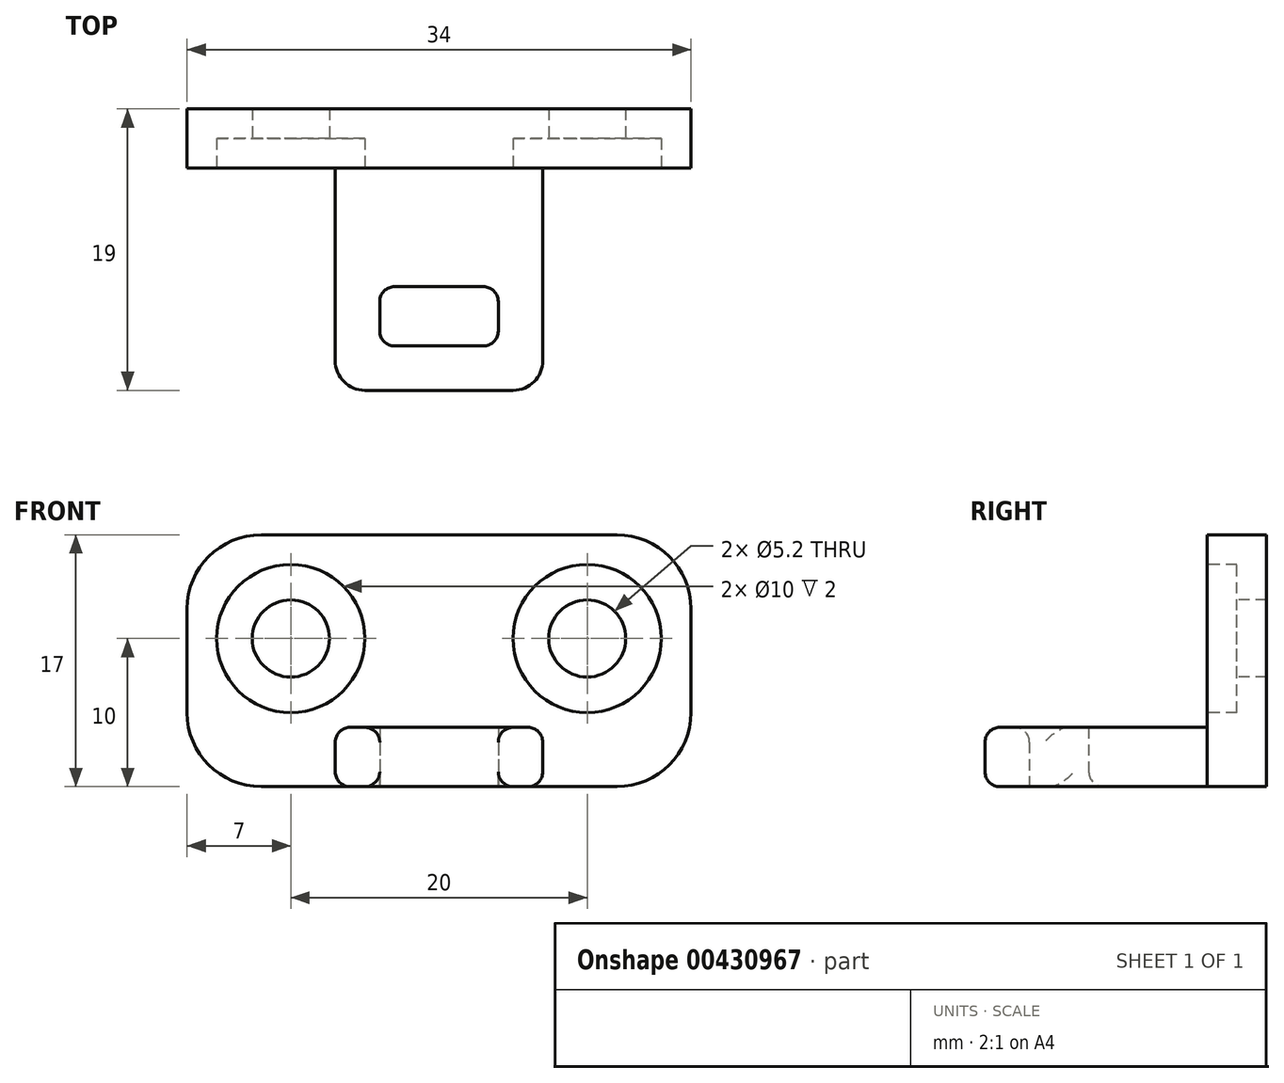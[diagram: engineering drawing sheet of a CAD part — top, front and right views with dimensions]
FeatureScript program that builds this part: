
annotation { "Feature Type Name" : "Feature", "Feature Type Description" : "" }
export const myFeature = defineFeature(function(context is Context, id is Id, definition is map)
    precondition{}
    {
        {
            var Q0;
            Q0=qCreatedBy(makeId("Top.planeOp"),FACE);
            var sketch = newSketch(context, id + "F0", { "sketchPlane" : qUnion([Q0])});
            skLineSegment(sketch, "E0.bottom", {"start": v(0, 0) * mm, "end": v(50, 0) * mm, "construction": true});
            skLineSegment(sketch, "E0.top", {"start": v(0, 20) * mm, "end": v(50, 20) * mm, "construction": true});
            skLineSegment(sketch, "E0.left", {"start": v(0, 0) * mm, "end": v(0, 20) * mm, "construction": true});
            skLineSegment(sketch, "E0.right", {"start": v(50, 0) * mm, "end": v(50, 20) * mm, "construction": true});
            skLineSegment(sketch, "E1.bottom", {"start": v(21, -8) * mm, "end": v(29, -8) * mm});
            skLineSegment(sketch, "E1.top", {"start": v(21, -12) * mm, "end": v(29, -12) * mm});
            skLineSegment(sketch, "E1.left", {"start": v(21, -8) * mm, "end": v(21, -12) * mm});
            skLineSegment(sketch, "E1.right", {"start": v(29, -8) * mm, "end": v(29, -12) * mm});
            skPoint(sketch, "E2", {"position": v(25, -8) * mm});
            skPoint(sketch, "E3", {"position": v(25, 0) * mm});
            skLineSegment(sketch, "E4.bottom", {"start": v(32, -15) * mm, "end": v(18, -15) * mm});
            skLineSegment(sketch, "E4.top", {"start": v(32, 0) * mm, "end": v(18, 0) * mm});
            skLineSegment(sketch, "E4.left", {"start": v(32, -15) * mm, "end": v(32, 0) * mm});
            skLineSegment(sketch, "E4.right", {"start": v(18, -15) * mm, "end": v(18, 0) * mm});
            skSolve(sketch);
        }
        {
            var Q0;
            Q0=makeQuery(id+"F0.imprint","IMPRINT",FACE,{"disambiguationData":[TD([[makeQuery(id+"F0.imprint","IMPRINT",EDGE,{"derivedFrom":sQuery(id+"F0.wireOp",EDGE,"E1.bottom")}),1.0]])]});
            extrude(context, id + "F1", {"entities" : qUnion([Q0]), "depth" : 4 * mm});
        }
        {
            var Q0;
            Q0=makeQuery(id+"F1.opExtrude","SWEPT_FACE",FACE,{"disambiguationData":[OSD([sQuery(id+"F0.wireOp",EDGE,"E4.top")])]});
            var sketch = newSketch(context, id + "F2", { "sketchPlane" : qUnion([Q0])});
            skLineSegment(sketch, "E5.bottom", {"start": v(0, 0) * mm, "end": v(-50, 0) * mm, "construction": true});
            skLineSegment(sketch, "E5.top", {"start": v(0, 20) * mm, "end": v(-50, 20) * mm, "construction": true});
            skLineSegment(sketch, "E5.left", {"start": v(0, 0) * mm, "end": v(0, 20) * mm, "construction": true});
            skLineSegment(sketch, "E5.right", {"start": v(-50, 0) * mm, "end": v(-50, 20) * mm, "construction": true});
            skPoint(sketch, "E6", {"position": v(0, 10) * mm});
            skLineSegment(sketch, "E7.bottom", {"start": v(-42, 0) * mm, "end": v(-8, 0) * mm});
            skLineSegment(sketch, "E7.top", {"start": v(-42, 17) * mm, "end": v(-8, 17) * mm});
            skLineSegment(sketch, "E7.left", {"start": v(-42, 0) * mm, "end": v(-42, 17) * mm});
            skLineSegment(sketch, "E7.right", {"start": v(-8, 0) * mm, "end": v(-8, 17) * mm});
            skPoint(sketch, "E8", {"position": v(-25, 17) * mm});
            skPoint(sketch, "E9", {"position": v(-15, 10) * mm});
            skPoint(sketch, "E10", {"position": v(-35, 10) * mm});
            skSolve(sketch);
        }
        {
            var Q0;
            Q0=makeQuery(id+"F2.imprint","IMPRINT",FACE,{"disambiguationData":[TD([[makeQuery(id+"F2.imprint","IMPRINT",EDGE,{"derivedFrom":sQuery(id+"F2.wireOp",EDGE,"E7.top")}),-1.0]])]});
            var Q1;
            {var subQ1=sQuery(id+"F0.wireOp",EDGE,"E4.top");Q1=makeQuery(id+"F2.imprint","IMPRINT",FACE,{"disambiguationData":[TD([[makeQuery(id+"F2.imprint","IMPRINT",EDGE,{"derivedFrom":makeQuery(id+"F1.opExtrude","CAP_EDGE",EDGE,{"disambiguationData":[OSD([subQ1])],"isStart":false})}),-1.0]])]});}
            extrude(context, id + "F3", {"entities" : qUnion([Q0, Q1]), "operationType" : NewBodyOperationType.ADD, "depth" : 4 * mm});
        }
        {
            var Q0;
            Q0=sQuery(id+"F2.wireOp",VERTEX,"E9");
            var Q1;
            Q1=sQuery(id+"F2.wireOp",VERTEX,"E10");
            var Q2;
            Q2=makeQuery(id+"F1.opExtrude","SWEPT_BODY",BODY,{"disambiguationData":[OSD([sQuery(id+"F0.wireOp",EDGE,"E1.bottom"),sQuery(id+"F0.wireOp",EDGE,"E1.top"),sQuery(id+"F0.wireOp",EDGE,"E1.left"),sQuery(id+"F0.wireOp",EDGE,"E1.right"),sQuery(id+"F0.wireOp",EDGE,"E4.bottom"),sQuery(id+"F0.wireOp",EDGE,"E4.top"),sQuery(id+"F0.wireOp",EDGE,"E4.left"),sQuery(id+"F0.wireOp",EDGE,"E4.right")])]});
            hole(context, id + "F4", {"style" : HoleStyle.C_BORE, "endStyle" : HoleEndStyle.THROUGH, "oppositeDirection" : true, "holeDiameter" : 5.2 * mm, "cBoreDiameter" : 10 * mm, "cBoreDepth" : 2 * mm, "tappedDepth" : 12 * mm, "tapClearance" : 3, "locations" : qUnion([Q0, Q1]), "scope" : qUnion([Q2])});
        }
        {
            var Q0;
            Q0=makeQuery(id+"F1.opExtrude","SWEPT_EDGE",EDGE,{"disambiguationData":[OSD([sQuery(id+"F0.wireOp",EDGE,"E4.bottom"),sQuery(id+"F0.wireOp",EDGE,"E4.right")])]});
            var Q1;
            Q1=makeQuery(id+"F1.opExtrude","SWEPT_EDGE",EDGE,{"disambiguationData":[OSD([sQuery(id+"F0.wireOp",EDGE,"E4.bottom"),sQuery(id+"F0.wireOp",EDGE,"E4.left")])]});
            fillet(context, id + "F5", {"entities" : qUnion([Q0, Q1]), "radius" : 2 * mm, "tangentPropagation" : true, "allowEdgeOverflow" : false});
        }
        {
            var Q0;
            Q0=makeQuery(id+"F1.opExtrude","SWEPT_EDGE",EDGE,{"disambiguationData":[OSD([sQuery(id+"F0.wireOp",EDGE,"E4.top"),sQuery(id+"F0.wireOp",EDGE,"E4.right")])]});
            var Q1;
            Q1=makeQuery(id+"F1.opExtrude","SWEPT_EDGE",EDGE,{"disambiguationData":[OSD([sQuery(id+"F0.wireOp",EDGE,"E4.top"),sQuery(id+"F0.wireOp",EDGE,"E4.left")])]});
            var Q2;
            Q2=makeQuery(id+"F1.opExtrude","CAP_EDGE",EDGE,{"disambiguationData":[OSD([sQuery(id+"F0.wireOp",EDGE,"E4.top")])],"isStart":false});
            var Q3;
            Q3=makeQuery(id+"F3.opExtrude","SWEPT_EDGE",EDGE,{"disambiguationData":[OSD([sQuery(id+"F2.wireOp",EDGE,"E7.top"),sQuery(id+"F2.wireOp",EDGE,"E7.left")])]});
            var Q4;
            Q4=makeQuery(id+"F3.opExtrude","SWEPT_EDGE",EDGE,{"disambiguationData":[OSD([sQuery(id+"F2.wireOp",EDGE,"E7.top"),sQuery(id+"F2.wireOp",EDGE,"E7.right")])]});
            var Q5;
            Q5=makeQuery(id+"F3.opExtrude","SWEPT_EDGE",EDGE,{"disambiguationData":[OSD([sQuery(id+"F2.wireOp",EDGE,"E7.bottom"),sQuery(id+"F2.wireOp",EDGE,"E7.left")])]});
            var Q6;
            Q6=makeQuery(id+"F3.opExtrude","SWEPT_EDGE",EDGE,{"disambiguationData":[OSD([sQuery(id+"F2.wireOp",EDGE,"E7.bottom"),sQuery(id+"F2.wireOp",EDGE,"E7.right")])]});
            fillet(context, id + "F6", {"entities" : qUnion([Q0, Q1, Q2, Q3, Q4, Q5, Q6]), "radius" : 5 * mm, "tangentPropagation" : true, "allowEdgeOverflow" : false});
        }
        {
            var Q0;
            Q0=makeQuery(id+"F1.opExtrude","SWEPT_EDGE",EDGE,{"disambiguationData":[OSD([sQuery(id+"F0.wireOp",EDGE,"E1.bottom"),sQuery(id+"F0.wireOp",EDGE,"E1.left")])]});
            var Q1;
            Q1=makeQuery(id+"F1.opExtrude","SWEPT_EDGE",EDGE,{"disambiguationData":[OSD([sQuery(id+"F0.wireOp",EDGE,"E1.bottom"),sQuery(id+"F0.wireOp",EDGE,"E1.right")])]});
            var Q2;
            Q2=makeQuery(id+"F1.opExtrude","SWEPT_EDGE",EDGE,{"disambiguationData":[OSD([sQuery(id+"F0.wireOp",EDGE,"E1.top"),sQuery(id+"F0.wireOp",EDGE,"E1.right")])]});
            var Q3;
            Q3=makeQuery(id+"F1.opExtrude","SWEPT_EDGE",EDGE,{"disambiguationData":[OSD([sQuery(id+"F0.wireOp",EDGE,"E1.top"),sQuery(id+"F0.wireOp",EDGE,"E1.left")])]});
            var Q4;
            Q4=makeQuery(id+"F1.opExtrude","CAP_EDGE",EDGE,{"disambiguationData":[OSD([sQuery(id+"F0.wireOp",EDGE,"E4.right")])],"isStart":false});
            var Q5;
            Q5=makeQuery(id+"F1.opExtrude","CAP_EDGE",EDGE,{"disambiguationData":[OSD([sQuery(id+"F0.wireOp",EDGE,"E1.top")])],"isStart":false});
            var Q6;
            Q6=makeQuery(id+"F1.opExtrude","CAP_EDGE",EDGE,{"disambiguationData":[OSD([sQuery(id+"F0.wireOp",EDGE,"E1.bottom")])],"isStart":true});
            var Q7;
            Q7=makeQuery(id+"F1.opExtrude","CAP_EDGE",EDGE,{"disambiguationData":[OSD([sQuery(id+"F0.wireOp",EDGE,"E4.bottom")])],"isStart":true});
            fillet(context, id + "F7", {"entities" : qUnion([Q0, Q1, Q2, Q3, Q4, Q5, Q6, Q7]), "radius" : 1 * mm, "tangentPropagation" : true, "allowEdgeOverflow" : false});
        }
    });
